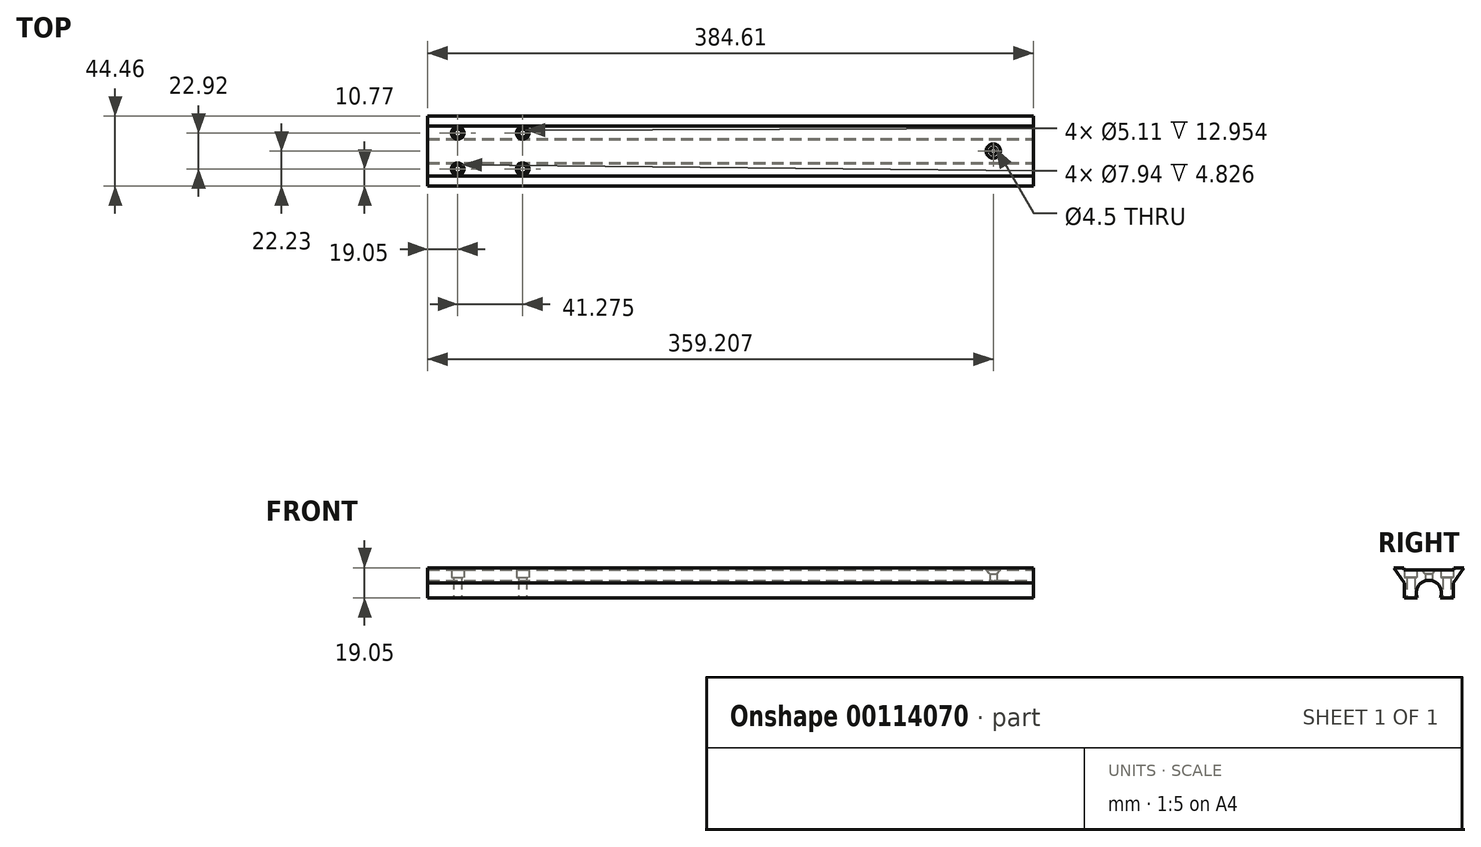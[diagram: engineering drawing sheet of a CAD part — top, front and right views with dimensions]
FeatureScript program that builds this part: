
annotation { "Feature Type Name" : "Feature", "Feature Type Description" : "" }
export const myFeature = defineFeature(function(context is Context, id is Id, definition is map)
    precondition{}
    {
        {
            var Q0;
            Q0=qCreatedBy(makeId("Front.planeOp"),FACE);
            var sketch = newSketch(context, id + "F0", { "sketchPlane" : qUnion([Q0])});
            skLineSegment(sketch, "E0", {"start": v(0, 36.78) * mm, "end": v(384.6, 36.78) * mm, "construction": true});
            skLineSegment(sketch, "E1", {"start": v(384.6, 36.78) * mm, "end": v(384.6, 55.83) * mm, "construction": true});
            skLineSegment(sketch, "E2", {"start": v(384.6, 55.83) * mm, "end": v(0, 55.83) * mm});
            skLineSegment(sketch, "E3", {"start": v(0, 55.83) * mm, "end": v(0, 36.78) * mm, "construction": true});
            skLineSegment(sketch, "E4", {"start": v(359.2, 55.83) * mm, "end": v(359.2, 36.78) * mm, "construction": true});
            skLineSegment(sketch, "E5", {"start": v(0, 0) * mm, "end": v(0, 36.78) * mm, "construction": true});
            skLineSegment(sketch, "E6", {"start": v(10.16, 55.83) * mm, "end": v(10.16, 36.78) * mm, "construction": true});
            skLineSegment(sketch, "E7", {"start": v(-94.6, 100.28) * mm, "end": v(252.4, 100.28) * mm, "construction": true});
            skLineSegment(sketch, "E8", {"start": v(0, 40.03) * mm, "end": v(270.04, 40.03) * mm, "construction": true});
            skLineSegment(sketch, "E9", {"start": v(38.1, 36.78) * mm, "end": v(38.1, 55.83) * mm, "construction": true});
            skSolve(sketch);
        }
        {
            var Q0;
            Q0=qCreatedBy(makeId("Right.planeOp"),FACE);
            var sketch = newSketch(context, id + "F1", { "sketchPlane" : qUnion([Q0])});
            skLineSegment(sketch, "E10", {"start": v(0, 54.56) * mm, "end": v(-15.87, 54.56) * mm});
            skLineSegment(sketch, "E11", {"start": v(-15.88, 54.56) * mm, "end": v(-15.88, 55.83) * mm});
            skLineSegment(sketch, "E12", {"start": v(-15.87, 55.83) * mm, "end": v(-22.23, 55.83) * mm});
            skLineSegment(sketch, "E13", {"start": v(-22.23, 55.83) * mm, "end": v(-15.68, 46.3) * mm});
            skLineSegment(sketch, "E14", {"start": v(-15.68, 46.3) * mm, "end": v(-15.68, 36.78) * mm});
            skLineSegment(sketch, "E15.MirrorCS", {"start": v(0, 54.56) * mm, "end": v(15.87, 54.56) * mm});
            skLineSegment(sketch, "E16.MirrorCS", {"start": v(15.88, 54.56) * mm, "end": v(15.88, 55.83) * mm});
            skLineSegment(sketch, "E17.MirrorCS", {"start": v(15.87, 55.83) * mm, "end": v(22.23, 55.83) * mm});
            skLineSegment(sketch, "E18.MirrorCS", {"start": v(22.23, 55.83) * mm, "end": v(15.68, 46.3) * mm});
            skLineSegment(sketch, "E19.MirrorCS", {"start": v(15.68, 46.3) * mm, "end": v(15.68, 36.78) * mm});
            skLineSegment(sketch, "E20.MirrorCS", {"start": v(15.68, 36.78) * mm, "end": v(7.24, 36.78) * mm});
            skLineSegment(sketch, "E21", {"start": v(-22.23, 55.83) * mm, "end": v(22.23, 55.83) * mm, "construction": true});
            skArc(sketch, "E22", {"start": v(7.24, 36.78) * mm, "mid": v(0, 47.97) * mm, "end": v(-7.24, 36.78) * mm});
            skLineSegment(sketch, "E23.trimOffspring", {"start": v(-7.24, 36.78) * mm, "end": v(-15.68, 36.78) * mm});
            skLineSegment(sketch, "E24", {"start": v(0, 36.78) * mm, "end": v(30.46, 36.78) * mm, "construction": true});
            skSolve(sketch);
        }
        {
            var Q0;
            Q0=makeQuery(id+"F1.imprint","IMPRINT",FACE,{"disambiguationData":[TD([[makeQuery(id+"F1.imprint","IMPRINT",EDGE,{"derivedFrom":sQuery(id+"F1.wireOp",EDGE,"E10")}),1.0]])]});
            var Q1;
            Q1=makeQuery(id+"F1.imprint","IMPRINT",FACE,{"disambiguationData":[TD([[makeQuery(id+"F1.imprint","IMPRINT",EDGE,{"derivedFrom":sQuery(id+"F1.wireOp",EDGE,"TZs2ILHc-WLRL-mXxZ-w2Cf-DeuHa6ZWfoBX")}),-1.0]])]});
            var Q2;
            Q2=sQuery(id+"F0.wireOp",EDGE,"E2");
            sweep(context, id + "F2", {"profiles" : qUnion([Q0, Q1]), "path" : qUnion([Q2])});
        }
        {
            var Q0;
            Q0=qCreatedBy(makeId("Top.planeOp"),FACE);
            var Q1;
            Q1=sQuery(id+"F0.wireOp",VERTEX,"E4.start");
            cPlane(context, id + "F3", {"entities" : qUnion([Q0, Q1]), "cplaneType" : CPlaneType.PLANE_POINT, "offset" : 152.4 * mm, "width" : 152.4 * mm, "height" : 152.4 * mm});
        }
        {
            var Q0;
            Q0=qCreatedBy(id+"F3.planeOp",FACE);
            var sketch = newSketch(context, id + "F4", { "sketchPlane" : qUnion([Q0])});
            skPoint(sketch, "E25", {"position": v(359.2, 0) * mm});
            skPoint(sketch, "E26", {"position": v(10.16, 0) * mm});
            skSolve(sketch);
        }
        {
            var Q0;
            Q0=sQuery(id+"F4.wireOp",VERTEX,"E25");
            var Q1;
            Q1=makeQuery(id+"F2.opSweep","SWEPT_BODY",BODY,{"disambiguationData":[OSD([sQuery(id+"F0.wireOp",EDGE,"E2"),sQuery(id+"F1.wireOp",EDGE,"E10"),sQuery(id+"F1.wireOp",EDGE,"E11"),sQuery(id+"F1.wireOp",EDGE,"E12"),sQuery(id+"F1.wireOp",EDGE,"E13"),sQuery(id+"F1.wireOp",EDGE,"E14"),sQuery(id+"F1.wireOp",EDGE,"X87oiVRN-ysOa-sD2N-sg38-9KkOZ4JYPg7D"),sQuery(id+"F1.wireOp",EDGE,"CL2VqxIS-GebI-aQCD-xlZQ-VNhWhIcAKvvh"),sQuery(id+"F1.wireOp",EDGE,"Zf8QREMj-DdWi-zZYj-mdpG-1FaBJpRE9Maa"),sQuery(id+"F1.wireOp",EDGE,"628a4c79-4e6e-448f-b028-d572425b52630.MirrorCS"),sQuery(id+"F1.wireOp",EDGE,"02f22541-65a7-40c5-8ece-0985ead0e49b0.MirrorCS"),sQuery(id+"F1.wireOp",EDGE,"1bc6c2b3-4a48-4f89-a437-c54f6313c6c00.MirrorCS"),sQuery(id+"F1.wireOp",EDGE,"3b4b1e3d-f0f6-47b1-98d0-925d0680fb270.MirrorCS"),sQuery(id+"F1.wireOp",EDGE,"b0615d98-6636-49bd-8cdd-ac4c00a9ebb20.MirrorCS"),sQuery(id+"F1.wireOp",EDGE,"a57a5671-f7d2-495c-b53b-6cc025fe254b0.MirrorCS"),sQuery(id+"F1.wireOp",EDGE,"d133d913-0c50-4157-9a9b-070efbd3cdf60.MirrorCS"),sQuery(id+"F1.wireOp",EDGE,"c2d840c5-71e9-4bd8-a8d9-9115f5aaefab0.MirrorCS")])]});
            hole(context, id + "F5", {"style" : HoleStyle.C_SINK, "holeDiameter" : 4.5 * mm, "cSinkDiameter" : 9.12 * mm, "endStyle" : HoleEndStyle.THROUGH, "locations" : qUnion([Q0]), "scope" : qUnion([Q1]), "cSinkAngle" : 82 * degree, "standardTappedOrClearance" : lookupTablePath({ "standard" : "ANSI", "fit" : "Normal (ASME)", "size" : "#8", "type" : "Clearance" }), "standardBlindInLast" : lookupTablePath({ "fit" : "Free", "standard" : "ANSI", "size" : "#8", "type" : "Clearance" }), "isTappedThrough" : true});
        }
        {
            var Q0;
            Q0=makeQuery(id+"F2.opSweep","CAP_FACE",FACE,{"disambiguationData":[OSD([sQuery(id+"F0.wireOp",VERTEX,"E2.start"),sQuery(id+"F1.wireOp",EDGE,"E10"),sQuery(id+"F1.wireOp",EDGE,"E11"),sQuery(id+"F1.wireOp",EDGE,"E12"),sQuery(id+"F1.wireOp",EDGE,"E13"),sQuery(id+"F1.wireOp",EDGE,"E14"),sQuery(id+"F1.wireOp",EDGE,"E15.MirrorCS"),sQuery(id+"F1.wireOp",EDGE,"E16.MirrorCS"),sQuery(id+"F1.wireOp",EDGE,"E17.MirrorCS"),sQuery(id+"F1.wireOp",EDGE,"E18.MirrorCS"),sQuery(id+"F1.wireOp",EDGE,"E19.MirrorCS"),sQuery(id+"F1.wireOp",EDGE,"E20.MirrorCS"),sQuery(id+"F1.wireOp",EDGE,"E22"),sQuery(id+"F1.wireOp",EDGE,"E23.trimOffspring")])],"isStart":false});
            var sketch = newSketch(context, id + "F6", { "sketchPlane" : qUnion([Q0])});
            skLineSegment(sketch, "E27", {"start": v(-15.87, 55.83) * mm, "end": v(15.87, 55.83) * mm, "construction": true});
            skPoint(sketch, "E28", {"position": v(0, 55.83) * mm});
            skSolve(sketch);
        }
        {
            var Q0;
            Q0=makeQuery(id+"F2.opSweep","SWEPT_FACE",FACE,{"disambiguationData":[OSD([sQuery(id+"F0.wireOp",EDGE,"E2"),sQuery(id+"F1.wireOp",EDGE,"E20.MirrorCS")])]});
            var sketch = newSketch(context, id + "F7", { "sketchPlane" : qUnion([Q0])});
            skLineSegment(sketch, "E29", {"start": v(60.33, 15.68) * mm, "end": v(60.33, 7.24) * mm, "construction": true});
            skPoint(sketch, "E30", {"position": v(60.33, 11.46) * mm});
            skLineSegment(sketch, "E31", {"start": v(19.05, 15.68) * mm, "end": v(19.05, 7.24) * mm, "construction": true});
            skPoint(sketch, "E32", {"position": v(19.05, 11.46) * mm});
            skSolve(sketch);
        }
        {
            var Q0;
            Q0=makeQuery(id+"F2.opSweep","SWEPT_FACE",FACE,{"disambiguationData":[OSD([sQuery(id+"F0.wireOp",EDGE,"E2"),sQuery(id+"F1.wireOp",EDGE,"E10"),sQuery(id+"F1.wireOp",EDGE,"E15.MirrorCS")])]});
            var sketch = newSketch(context, id + "F8", { "sketchPlane" : qUnion([Q0])});
            skPoint(sketch, "E33", {"position": v(60.33, -11.46) * mm});
            skPoint(sketch, "E34", {"position": v(19.05, -11.46) * mm});
            skPoint(sketch, "E35.MirrorP", {"position": v(60.33, 11.46) * mm});
            skPoint(sketch, "E36.MirrorP", {"position": v(19.05, 11.46) * mm});
            skSolve(sketch);
        }
        {
            var Q0;
            Q0=sQuery(id+"F8.wireOp",VERTEX,"E35.MirrorP");
            var Q1;
            Q1=sQuery(id+"F8.wireOp",VERTEX,"E33");
            var Q2;
            Q2=sQuery(id+"F8.wireOp",VERTEX,"E34");
            var Q3;
            Q3=sQuery(id+"F8.wireOp",VERTEX,"E36.MirrorP");
            var Q4;
            Q4=makeQuery(id+"F2.opSweep","SWEPT_BODY",BODY,{"disambiguationData":[OSD([sQuery(id+"F0.wireOp",EDGE,"E2"),sQuery(id+"F1.wireOp",EDGE,"E10"),sQuery(id+"F1.wireOp",EDGE,"E11"),sQuery(id+"F1.wireOp",EDGE,"E12"),sQuery(id+"F1.wireOp",EDGE,"E13"),sQuery(id+"F1.wireOp",EDGE,"E14"),sQuery(id+"F1.wireOp",EDGE,"E15.MirrorCS"),sQuery(id+"F1.wireOp",EDGE,"E16.MirrorCS"),sQuery(id+"F1.wireOp",EDGE,"E17.MirrorCS"),sQuery(id+"F1.wireOp",EDGE,"E18.MirrorCS"),sQuery(id+"F1.wireOp",EDGE,"E19.MirrorCS"),sQuery(id+"F1.wireOp",EDGE,"E20.MirrorCS"),sQuery(id+"F1.wireOp",EDGE,"E22"),sQuery(id+"F1.wireOp",EDGE,"E23.trimOffspring")])]});
            hole(context, id + "F9", {"style" : HoleStyle.C_BORE, "endStyle" : HoleEndStyle.THROUGH, "holeDiameter" : 5.1 * mm, "cBoreDiameter" : 7.94 * mm, "cBoreDepth" : 4.83 * mm, "locations" : qUnion([Q0, Q1, Q2, Q3]), "scope" : qUnion([Q4]), "isTappedThrough" : true});
        }
    });
